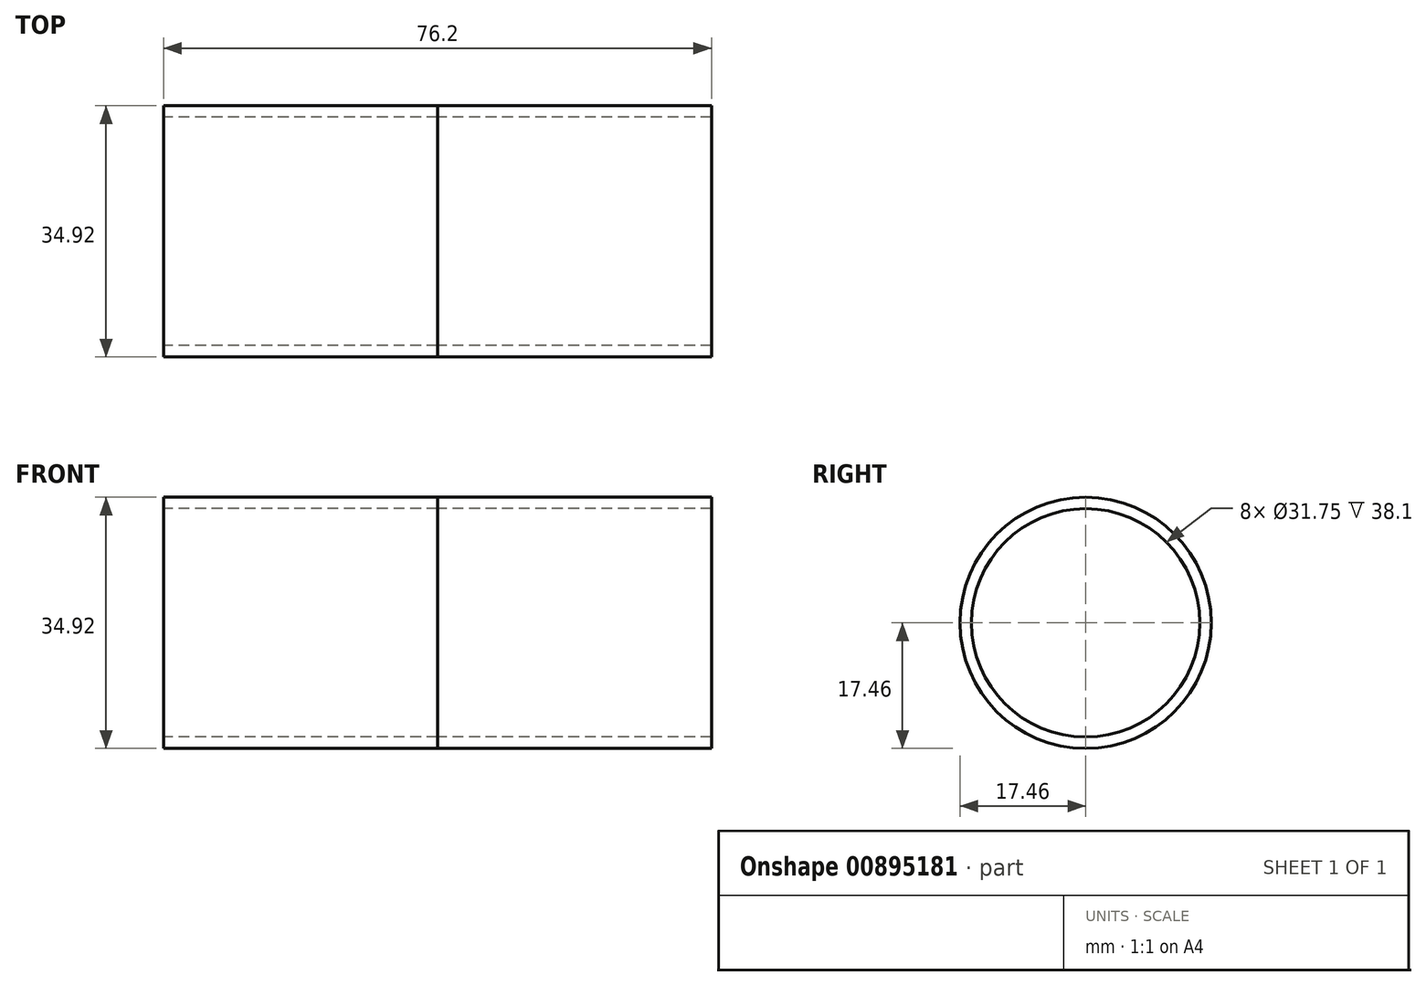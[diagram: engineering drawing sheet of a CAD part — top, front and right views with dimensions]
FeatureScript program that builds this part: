
annotation { "Feature Type Name" : "Feature", "Feature Type Description" : "" }
export const myFeature = defineFeature(function(context is Context, id is Id, definition is map)
    precondition{}
    {
        {
            var Q0;
            Q0=qCreatedBy(makeId("Right.planeOp"),FACE);
            var sketch = newSketch(context, id + "F0", { "sketchPlane" : qUnion([Q0])});
            skCircle(sketch, "E0", {"center": v(0, 0) * mm, "radius": 15.88 * mm});
            skCircle(sketch, "E1", {"center": v(0, 0) * mm, "radius": 17.46 * mm});
            skSolve(sketch);
        }
        {
            var Q0;
            Q0=qSketchRegion(id+"F0",true);
            extrude(context, id + "F1", {"entities" : qUnion([Q0]), "depth" : 38.1 * mm, "offsetDistance" : 25 * mm});
        }
        {
            var Q0;
            Q0=makeQuery(id+"F1.opExtrude","CAP_FACE",FACE,{"disambiguationData":[OSD([sQuery(id+"F0.wireOp",EDGE,"E0"),sQuery(id+"F0.wireOp",EDGE,"E1")])],"isStart":false});
            var sketch = newSketch(context, id + "F2", { "sketchPlane" : qUnion([Q0])});
            skCircle(sketch, "E2", {"center": v(0, 0) * mm, "radius": 15.88 * mm});
            skCircle(sketch, "E3", {"center": v(0, 0) * mm, "radius": 17.46 * mm});
            skSolve(sketch);
        }
        {
            var Q0;
            Q0=qSketchRegion(id+"F2",true);
            extrude(context, id + "F3", {"entities" : qUnion([Q0]), "depth" : 38.1 * mm, "offsetDistance" : 25 * mm});
        }
    });
